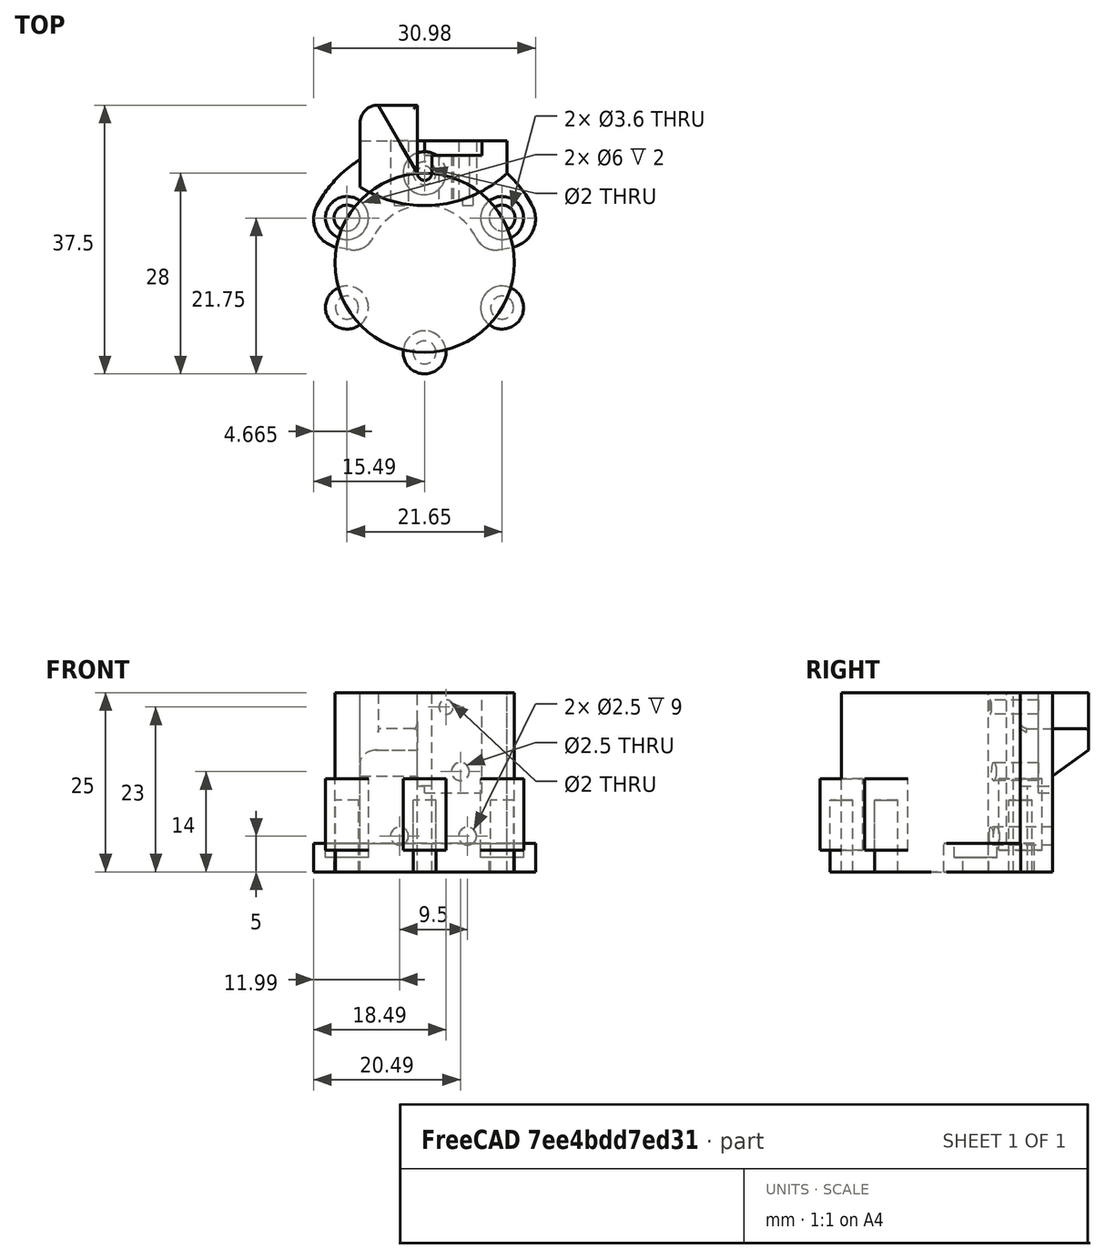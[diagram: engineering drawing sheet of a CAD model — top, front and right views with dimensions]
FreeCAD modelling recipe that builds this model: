
FCSTD DOCUMENT  (FreeCAD 0.14R3703 (Git))
Label: GOUM_Center6
License: CC-BY 3.0
LicenseURL: http://creativecommons.org/licenses/by/3.0/
objects: Part::Cylinder×29, Part::Cut×25, Part::Box×9, Part::Part2DObjectPython×3, Part::MultiFuse×3, Part::Fillet×3
note: 72 computed .brp shape members not serialized (recipe doc carries the construction recipe); baked Part::Feature solids carry a one-line shape summary decoded from their .brp

FEATURE [Part::Part2DObjectPython] Circle  label="DO_NOT_PRINT_Circle12.5"  # Draft 2D object (typed FeaturePython)
  FirstAngle = 0
  LastAngle = 360
  MakeFace = false
  Radius = 12.5
FEATURE [Part::Cylinder] Cylinder  label="DO_NOT_PRINT_Cylinder0_M3"
  Angle = 360
  Height = 10
  Placement = pos=(0,12.5,0) rot=(0,0,1;0rad)
  Radius = 1.6
FEATURE [Part::Cylinder] Cylinder001  label="Cylinder60"
  Angle = 360
  Height = 10
  Placement = pos=(10.825,6.25,0) rot=(0,0,1;0rad)
  Radius = 1.8
FEATURE [Part::Cylinder] Cylinder002  label="DO_NOT_PRINT_Cylinder120"
  Angle = 360
  Height = 10
  Placement = pos=(10.825,-6.25,0) rot=(0,0,1;0rad)
  Radius = 1.6
FEATURE [Part::Cylinder] Cylinder003  label="DO_NOT_PRINT_Cylinder180"
  Angle = 360
  Height = 10
  Placement = pos=(0,-12.5,0) rot=(0,0,1;0rad)
  Radius = 1.6
FEATURE [Part::Cylinder] Cylinder004  label="DO_NOT_PRINT_Cylinder240"
  Angle = 360
  Height = 10
  Placement = pos=(-10.825,-6.25,0) rot=(0,0,1;0rad)
  Radius = 1.6
FEATURE [Part::Cylinder] Cylinder005  label="Cylinder300"
  Angle = 360
  Height = 10
  Placement = pos=(-10.825,6.25,0) rot=(0,0,1;0rad)
  Radius = 1.8
FEATURE [Part::Cylinder] Cylinder006  label="CylinderCenter"
  Angle = 360
  Height = 25
  Radius = 8
FEATURE [Part::Cylinder] Cylinder007  label="DO_NOT_PRINT_Cylinder0_M55"
  Angle = 360
  Height = 10
  Placement = pos=(0,12.5,3) rot=(0,0,1;0rad)
  Radius = 3
FEATURE [Part::Cylinder] Cylinder008  label="Cylinder60_M55"
  Angle = 360
  Height = 2
  Placement = pos=(10.825,6.25,2) rot=(0,0,1;0rad)
  Radius = 3
FEATURE [Part::Cylinder] Cylinder009  label="DO_NOT_PRINT_Cylinder120_M55"
  Angle = 360
  Height = 10
  Placement = pos=(10.825,-6.25,3) rot=(0,0,1;0rad)
  Radius = 3
FEATURE [Part::Cylinder] Cylinder010  label="DO_NOT_PRINT_Cylinder180_M55"
  Angle = 360
  Height = 10
  Placement = pos=(0,-12.5,3) rot=(0,0,1;0rad)
  Radius = 3
FEATURE [Part::Cylinder] Cylinder011  label="DO_NOT_PRINT_Cylinder240_M55"
  Angle = 360
  Height = 10
  Placement = pos=(-10.825,-6.25,3) rot=(0,0,1;0rad)
  Radius = 3
FEATURE [Part::Cylinder] Cylinder012  label="Cylinder300_M55"
  Angle = 360
  Height = 2
  Placement = pos=(-10.825,6.25,2) rot=(0,0,1;0rad)
  Radius = 3
FEATURE [Part::Cylinder] Cylinder013  label="Cylinder0_M2"
  Angle = 360
  Height = 25
  Placement = pos=(0,12.5,0) rot=(0,0,1;0rad)
  Radius = 1
FEATURE [Part::Part2DObjectPython] Circle001  label="DO_NOT_PRINT_Circle17"  # Draft 2D object (typed FeaturePython)
  FirstAngle = 0
  LastAngle = 360
  MakeFace = false
  Radius = 17
FEATURE [Part::Cylinder] Cylinder014  label="HalfCylinderEffectorMax"
  Angle = 180
  Height = 25
  Radius = 17
FEATURE [Part::Cylinder] Cylinder015  label="DO_NOT_PRINT_Cylinder12.5"
  Angle = 360
  Height = 25
  Radius = 12.5
FEATURE [Part::Box] Box003  label="CubeRight"
  Height = 25
  Length = 20
  Placement = pos=(8,0,4) rot=(0,0,1;0rad)
  Width = 20
FEATURE [Part::Box] Box004  label="CubeLeft"
  Height = 25
  Length = 20
  Placement = pos=(-28,0,4) rot=(0,0,1;0rad)
  Width = 20
FEATURE [Part::Box] Box005  label="CubeBody"
  Height = 25
  Length = 20.5
  Placement = pos=(-9,8,0) rot=(0,0,1;0rad)
  Width = 9
FEATURE [Part::Box] Box006  label="CubeSlot"
  Height = 25
  Length = 2
  Placement = pos=(-1,12.5,12) rot=(0,0,1;0rad)
  Width = 10
FEATURE [Part::Part2DObjectPython] Circle002  label="DO_NOT_PRINT_Circle8"  # Draft 2D object (typed FeaturePython)
  FirstAngle = 0
  LastAngle = 360
  MakeFace = false
  Radius = 8
FEATURE [Part::Cylinder] Cylinder018  label="Cylinder302"
  Angle = 10
  Height = 10
  Radius = 17
FEATURE [Part::Cylinder] Cylinder019  label="Cylinder303"
  Angle = 10
  Height = 10
  Radius = 8
FEATURE [Part::Cylinder] Cylinder020  label="Cylinder304"
  Angle = 10
  Height = 10
  Placement = pos=(0,0,0) rot=(0,0,1;2.96706rad)
  Radius = 17
FEATURE [Part::Cylinder] Cylinder021  label="Cylinder305"
  Angle = 10
  Height = 10
  Placement = pos=(0,0,0) rot=(0,0,1;2.96706rad)
  Radius = 8
FEATURE [Part::Cut] Cut012  label="DeltaRight"
  Base = -> Cylinder018
  Tool = -> Cylinder019
FEATURE [Part::Cut] Cut013  label="DeltaLeft"
  Base = -> Cylinder020
  Tool = -> Cylinder021
FEATURE [Part::Cylinder] Cylinder023  label="CylinderSwitchLeft"
  Angle = 360
  Height = 20
  Placement = pos=(6,28,5) rot=(1,0,0;1.5708rad)
  Radius = 1.25
FEATURE [Part::Cylinder] Cylinder025  label="CylinderSpringBottom"
  Angle = 360
  Height = 20
  Placement = pos=(5,28,14) rot=(1,0,0;1.5708rad)
  Radius = 1.25
FEATURE [Part::Cylinder] Cylinder026  label="CylinderSpringTop"
  Angle = 360
  Height = 20
  Placement = pos=(3,28,23) rot=(1,0,0;1.5708rad)
  Radius = 1
FEATURE [Part::Box] Box007  label="CubeBack"
  Height = 25
  Length = 20
  Placement = pos=(-10,-8,4) rot=(0,0,1;0rad)
  Width = 16
FEATURE [Part::Cylinder] Cylinder027  label="Cylinder307"
  Angle = 360
  Height = 25
  Placement = pos=(0,25,4) rot=(0,0,1;0rad)
  Radius = 17
FEATURE [Part::Cylinder] Cylinder028  label="Cylinder308"
  Angle = 360
  Height = 25
  Placement = pos=(0,25,4) rot=(0,0,1;0rad)
  Radius = 25
FEATURE [Part::Cut] Cut031  label="BackCut"
  Base = -> Cylinder028
  Tool = -> Cylinder027
FEATURE [Part::Cylinder] Cylinder024  label="CylinderSwitchRight"
  Angle = 360
  Height = 20
  Placement = pos=(-3.5,28,5) rot=(1,0,0;1.5708rad)
  Radius = 1.25
FEATURE [Part::Box] Box008  label="SpringRecess"
  Height = 15
  Length = 8
  Placement = pos=(0,15,11) rot=(0,0,1;0rad)
  Width = 2
FEATURE [Part::Box] Box009  label="CubeProbeStop"
  Height = 8
  Length = 10
  Placement = pos=(-9,17,17) rot=(0,0,1;0rad)
  Width = 5
FEATURE [Part::Cylinder] Cylinder029  label="ClickSlot"
  Angle = 30
  Height = 10
  Placement = pos=(-1,12.5,20) rot=(0,0,1;1.5708rad)
  Radius = 15
FEATURE [Part::Cut] Cut
  Base = -> Cylinder014
  Tool = -> Cylinder006
FEATURE [Part::Cut] Cut032
  Base = -> Cut
  Tool = -> Box003
FEATURE [Part::Cut] Cut033
  Base = -> Cut032
  Tool = -> Box004
FEATURE [Part::Cut] Cut034
  Base = -> Cut033
  Tool = -> Cut013
FEATURE [Part::Cut] Cut035
  Base = -> Cut034
  Tool = -> Cut012
FEATURE [Part::Cut] Cut036
  Base = -> Cut035
  Tool = -> Box007
FEATURE [Part::MultiFuse] Fusion
  Shapes = -> [Cut036,Box005]
FEATURE [Part::MultiFuse] Fusion001
  Shapes = -> [Fusion,Box009]
FEATURE [Part::Cut] Cut037
  Base = -> Fusion001
  Tool = -> Box006
FEATURE [Part::Cut] Cut038
  Base = -> Cut037
  Tool = -> Cylinder029
FEATURE [Part::Cut] Cut039
  Base = -> Cut038
  Tool = -> Box008
FEATURE [Part::Cut] Cut040
  Base = -> Cut039
  Tool = -> Cylinder013
FEATURE [Part::Cut] Cut041
  Base = -> Cut040
  Tool = -> Cylinder005
FEATURE [Part::Cut] Cut042
  Base = -> Cut041
  Tool = -> Cylinder001
FEATURE [Part::Cut] Cut043
  Base = -> Cut042
  Tool = -> Cylinder012
FEATURE [Part::Cut] Cut044
  Base = -> Cut043
  Tool = -> Cylinder008
FEATURE [Part::Cut] Cut045
  Base = -> Cut044
  Tool = -> Cylinder024
FEATURE [Part::Cut] Cut046
  Base = -> Cut045
  Tool = -> Cylinder023
FEATURE [Part::Cut] Cut047
  Base = -> Cut046
  Tool = -> Cylinder025
FEATURE [Part::Cut] Cut048
  Base = -> Cut047
  Tool = -> Cylinder026
FEATURE [Part::Cut] Cut049
  Base = -> Cut048
  Tool = -> Cut031
FEATURE [Part::Fillet] Fillet
  Base = -> Cut049
  Edges = 2 edges r=3: [Edge128,Edge154]
FEATURE [Part::Fillet] Fillet001
  Base = -> Fillet
  Edges = 2 edges r=4: [Edge23,Edge107]
FEATURE [Part::Fillet] Fillet002
  Base = -> Fillet001
  Edges = 2 edges r=0.5: [Edge137,Edge150]
FEATURE [Part::Box] Box  label="Cube"
  Height = 9
  Length = 8
  Placement = pos=(-9,27,12) rot=(1,0,0;2.19911rad)
  Width = 7
FEATURE [Part::Box] Box010  label="Cube001"
  Height = 5
  Length = 8
  Placement = pos=(-9,17,12) rot=(0,0,1;0rad)
  Width = 5
FEATURE [Part::Cut] Cut050
  Base = -> Box010
  Tool = -> Box
FEATURE [Part::MultiFuse] Fusion002
  Shapes = -> [Fillet002,Cut050]
FEATURE [Part::Cylinder] Cylinder030  label="Cylinder"
  Angle = 90
  Height = 10
  Radius = 2.5
FEATURE [Part::Cylinder] Cylinder031  label="Cylinder309"
  Angle = 90
  Height = 10
  Radius = 5
FEATURE [Part::Cut] Cut051
  Base = -> Cylinder031
  Placement = pos=(-6.5,19.5,15) rot=(0,0,1;1.5708rad)
  Tool = -> Cylinder030
FEATURE [Part::Cut] Cut052  label="Z-Probe-holder"
  Base = -> Fusion002
  Tool = -> Cut051
